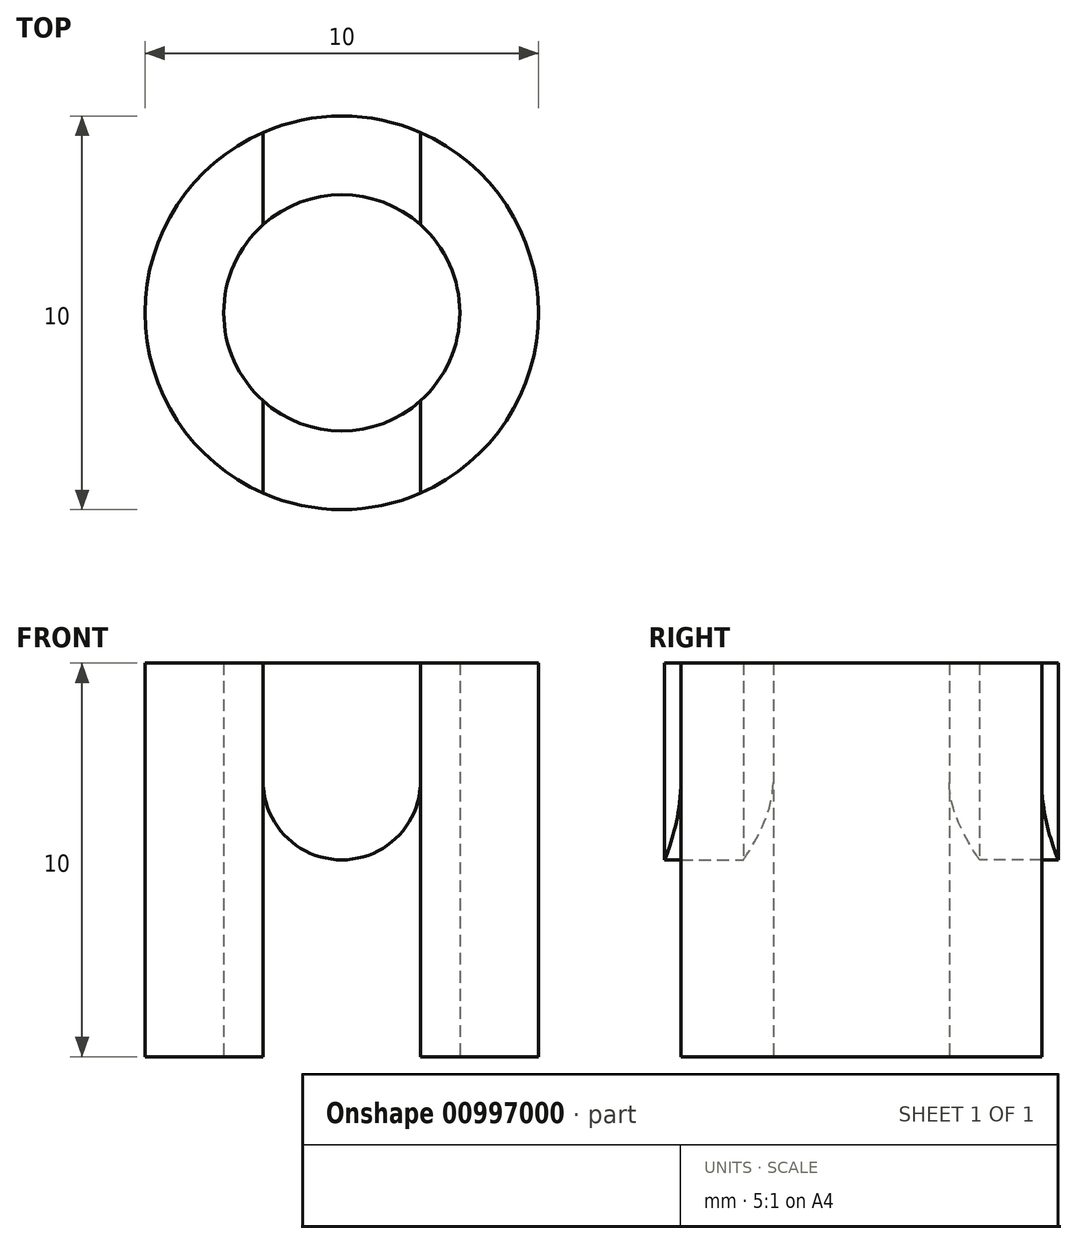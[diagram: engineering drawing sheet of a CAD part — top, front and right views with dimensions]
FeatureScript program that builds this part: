
annotation { "Feature Type Name" : "Feature", "Feature Type Description" : "" }
export const myFeature = defineFeature(function(context is Context, id is Id, definition is map)
    precondition{}
    {
        {
            var Q0;
            Q0=qCreatedBy(makeId("Top.planeOp"),FACE);
            var sketch = newSketch(context, id + "F0", { "sketchPlane" : qUnion([Q0])});
            skCircle(sketch, "E0", {"center": v(0, 0) * mm, "radius": 3 * mm});
            skCircle(sketch, "E1", {"center": v(0, 0) * mm, "radius": 5 * mm});
            skLineSegment(sketch, "E2", {"start": v(-2, 6.14) * mm, "end": v(-2, -7.68) * mm});
            skLineSegment(sketch, "E3", {"start": v(2, 6.08) * mm, "end": v(2, -7.54) * mm});
            skSolve(sketch);
        }
        {
            var Q0;
            {var subQ0=sQuery(id+"F0.wireOp",EDGE,"E2");var subQ1=sQuery(id+"F0.wireOp",EDGE,"E0");var subQ2=makeQuery(id+"F0.imprint","INTERSECT",VERTEX,{"disambiguationData":[OD(0.0)],"derivedFrom":[subQ1,subQ0]});Q0=makeQuery(id+"F0.imprint","IMPRINT",FACE,{"disambiguationData":[TD([[makeQuery(id+"F0.imprint","IMPRINT",EDGE,{"disambiguationData":[TD([[subQ2,-1.0]])],"derivedFrom":subQ1}),-1.0]])]});}
            var Q1;
            {var subQ0=sQuery(id+"F0.wireOp",EDGE,"E3");var subQ1=sQuery(id+"F0.wireOp",EDGE,"E0");var subQ2=makeQuery(id+"F0.imprint","INTERSECT",VERTEX,{"disambiguationData":[OD(0.0)],"derivedFrom":[subQ1,subQ0]});Q1=makeQuery(id+"F0.imprint","IMPRINT",FACE,{"disambiguationData":[TD([[makeQuery(id+"F0.imprint","IMPRINT",EDGE,{"disambiguationData":[TD([[subQ2,1.0]])],"derivedFrom":subQ1}),-1.0]])]});}
            extrude(context, id + "F1", {"entities" : qUnion([Q0, Q1]), "depth" : 10 * mm, "offsetDistance" : 25 * mm});
        }
        {
            var Q0;
            {var subQ0=sQuery(id+"F0.wireOp",EDGE,"E2");var subQ1=sQuery(id+"F0.wireOp",EDGE,"E0");var subQ2=makeQuery(id+"F0.imprint","INTERSECT",VERTEX,{"disambiguationData":[OD(1.0)],"derivedFrom":[subQ1,subQ0]});Q0=makeQuery(id+"F0.imprint","IMPRINT",FACE,{"disambiguationData":[TD([[makeQuery(id+"F0.imprint","IMPRINT",EDGE,{"disambiguationData":[TD([[subQ2,-1.0]])],"derivedFrom":subQ1}),-1.0]])]});}
            var Q1;
            {var subQ0=sQuery(id+"F0.wireOp",EDGE,"E2");var subQ1=sQuery(id+"F0.wireOp",EDGE,"E0");var subQ2=makeQuery(id+"F0.imprint","INTERSECT",VERTEX,{"disambiguationData":[OD(0.0)],"derivedFrom":[subQ1,subQ0]});Q1=makeQuery(id+"F0.imprint","IMPRINT",FACE,{"disambiguationData":[TD([[makeQuery(id+"F0.imprint","IMPRINT",EDGE,{"disambiguationData":[TD([[subQ2,1.0]])],"derivedFrom":subQ1}),-1.0]])]});}
            extrude(context, id + "F2", {"entities" : qUnion([Q0, Q1]), "depth" : 10 * mm, "offsetDistance" : 25 * mm, "hasSecondDirection" : true, "secondDirectionOppositeDirection" : false, "secondDirectionDepth" : 5 * mm});
        }
        {
            var Q0;
            {var subQ0=sQuery(id+"F0.wireOp",EDGE,"E2");Q0=makeQuery(id+"F2.opExtrude","CAP_EDGE",EDGE,{"disambiguationData":[OSD([subQ0]),TDD([makeQuery(id+"F0.imprint","IMPRINT",EDGE,{"disambiguationData":[TD([[makeQuery(id+"F0.imprint","INTERSECT",VERTEX,{"disambiguationData":[OD(0.0)],"derivedFrom":[sQuery(id+"F0.wireOp",EDGE,"E1"),subQ0]}),-1.0]])],"derivedFrom":subQ0})])],"isStart":true});}
            var Q1;
            {var subQ0=sQuery(id+"F0.wireOp",EDGE,"E3");Q1=makeQuery(id+"F2.opExtrude","CAP_EDGE",EDGE,{"disambiguationData":[OSD([subQ0]),TDD([makeQuery(id+"F0.imprint","IMPRINT",EDGE,{"disambiguationData":[TD([[makeQuery(id+"F0.imprint","INTERSECT",VERTEX,{"disambiguationData":[OD(0.0)],"derivedFrom":[sQuery(id+"F0.wireOp",EDGE,"E1"),subQ0]}),-1.0]])],"derivedFrom":subQ0})])],"isStart":true});}
            var Q2;
            {var subQ0=sQuery(id+"F0.wireOp",EDGE,"E3");Q2=makeQuery(id+"F2.opExtrude","CAP_EDGE",EDGE,{"disambiguationData":[OSD([subQ0]),TDD([makeQuery(id+"F0.imprint","IMPRINT",EDGE,{"disambiguationData":[TD([[makeQuery(id+"F0.imprint","INTERSECT",VERTEX,{"disambiguationData":[OD(1.0)],"derivedFrom":[sQuery(id+"F0.wireOp",EDGE,"E1"),subQ0]}),1.0]])],"derivedFrom":subQ0})])],"isStart":true});}
            var Q3;
            {var subQ0=sQuery(id+"F0.wireOp",EDGE,"E2");Q3=makeQuery(id+"F2.opExtrude","CAP_EDGE",EDGE,{"disambiguationData":[OSD([subQ0]),TDD([makeQuery(id+"F0.imprint","IMPRINT",EDGE,{"disambiguationData":[TD([[makeQuery(id+"F0.imprint","INTERSECT",VERTEX,{"disambiguationData":[OD(1.0)],"derivedFrom":[sQuery(id+"F0.wireOp",EDGE,"E1"),subQ0]}),1.0]])],"derivedFrom":subQ0})])],"isStart":true});}
            fillet(context, id + "F3", {"entities" : qUnion([Q0, Q1, Q2, Q3]), "radius" : 2 * mm, "tangentPropagation" : true, "allowEdgeOverflow" : false});
        }
    });
